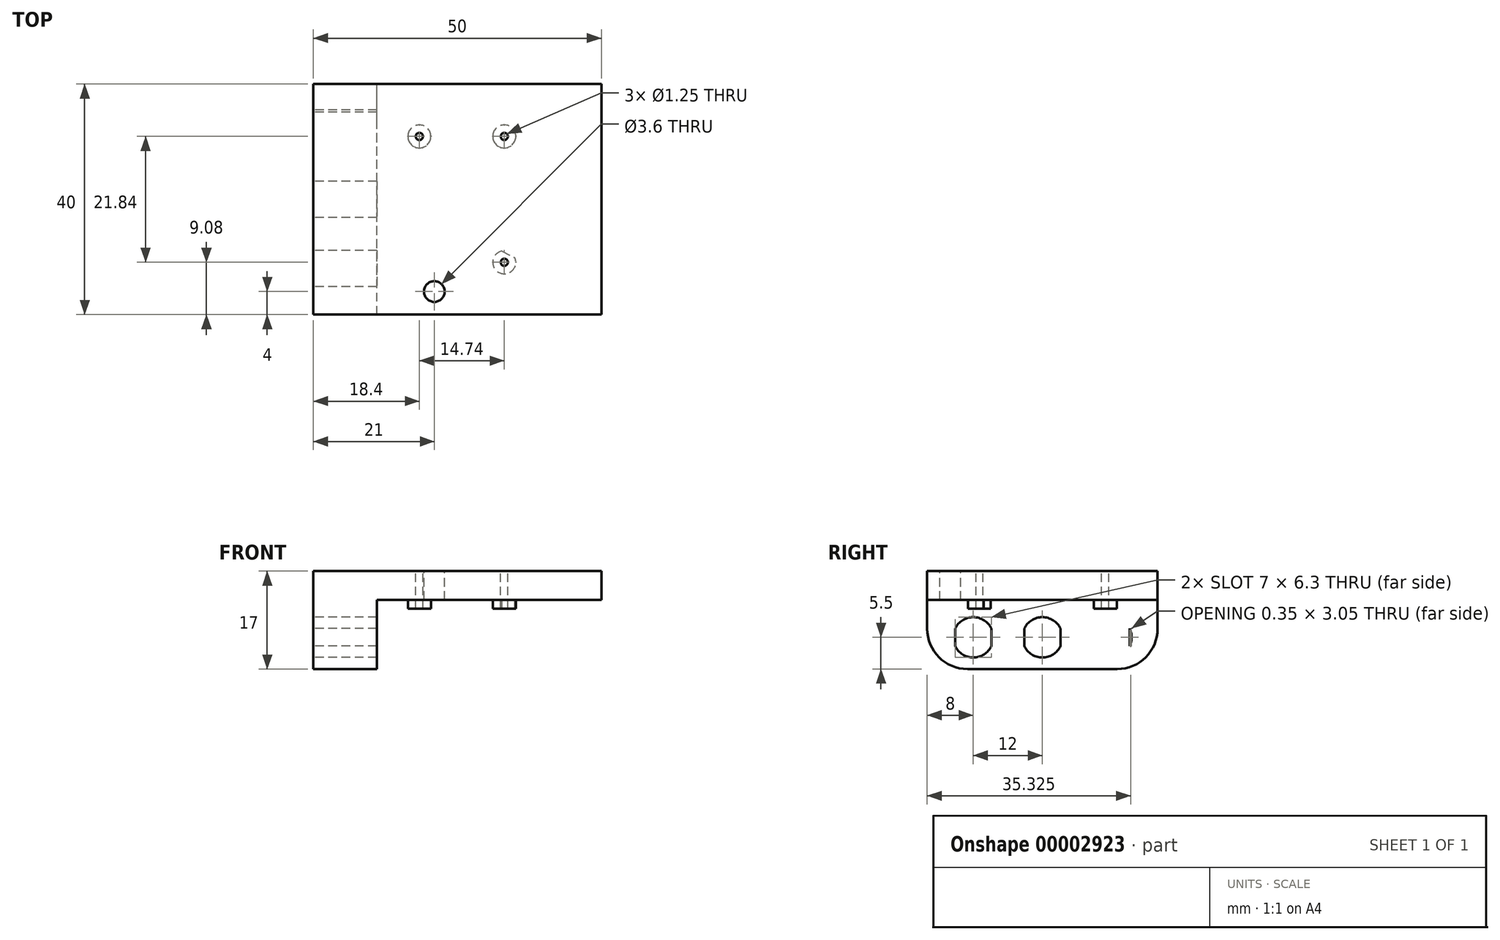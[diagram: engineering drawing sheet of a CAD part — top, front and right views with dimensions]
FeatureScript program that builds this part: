
annotation { "Feature Type Name" : "Feature", "Feature Type Description" : "" }
export const myFeature = defineFeature(function(context is Context, id is Id, definition is map)
    precondition{}
    {
        {
            var Q0;
            Q0=qCreatedBy(makeId("Top.planeOp"),FACE);
            var sketch = newSketch(context, id + "F0", { "sketchPlane" : qUnion([Q0])});
            skLineSegment(sketch, "E0.rect.bottom", {"start": v(25, 20) * mm, "end": v(-25, 20) * mm});
            skLineSegment(sketch, "E0.rect.top", {"start": v(25, -20) * mm, "end": v(-25, -20) * mm});
            skLineSegment(sketch, "E0.rect.left", {"start": v(25, 20) * mm, "end": v(25, -20) * mm});
            skLineSegment(sketch, "E0.rect.right", {"start": v(-25, 20) * mm, "end": v(-25, -20) * mm});
            skPoint(sketch, "E0.rect.middle", {"position": v(0, 0) * mm});
            skSolve(sketch);
        }
        {
            var Q0;
            Q0=makeQuery(id+"F0.imprint","IMPRINT",FACE,{"disambiguationData":[TD([[makeQuery(id+"F0.imprint","IMPRINT",EDGE,{"derivedFrom":sQuery(id+"F0.wireOp",EDGE,"E0.rect.bottom")}),1.0]])]});
            extrude(context, id + "F1", {"entities" : qUnion([Q0]), "depth" : 5 * mm});
        }
        {
            var Q0;
            Q0=makeQuery(id+"F1.opExtrude","CAP_FACE",FACE,{"disambiguationData":[OSD([sQuery(id+"F0.wireOp",EDGE,"E0.rect.bottom"),sQuery(id+"F0.wireOp",EDGE,"E0.rect.top"),sQuery(id+"F0.wireOp",EDGE,"E0.rect.left"),sQuery(id+"F0.wireOp",EDGE,"E0.rect.right")])],"isStart":false});
            var sketch = newSketch(context, id + "F2", { "sketchPlane" : qUnion([Q0])});
            skCircle(sketch, "E1", {"center": v(8.14, -10.92) * mm, "radius": 0.63 * mm});
            skCircle(sketch, "E2", {"center": v(8.14, 10.92) * mm, "radius": 0.63 * mm});
            skCircle(sketch, "E3", {"center": v(-6.6, 10.92) * mm, "radius": 0.63 * mm});
            skCircle(sketch, "E4", {"center": v(-4, -16) * mm, "radius": 1.8 * mm});
            skSolve(sketch);
        }
        {
            var Q0;
            Q0 = qSketchRegion(id + "F2", true);
            extrude(context, id + "F3", {"entities" : qUnion([Q0]), "operationType" : NewBodyOperationType.REMOVE, "oppositeDirection" : true, "depth" : 25 * mm});
        }
        {
            var Q0;
            Q0=makeQuery(id+"F1.opExtrude","CAP_FACE",FACE,{"disambiguationData":[OSD([sQuery(id+"F0.wireOp",EDGE,"E0.rect.bottom"),sQuery(id+"F0.wireOp",EDGE,"E0.rect.top"),sQuery(id+"F0.wireOp",EDGE,"E0.rect.left"),sQuery(id+"F0.wireOp",EDGE,"E0.rect.right")])],"isStart":true});
            var sketch = newSketch(context, id + "F4", { "sketchPlane" : qUnion([Q0])});
            skLineSegment(sketch, "E5.bottom", {"start": v(-25, 20) * mm, "end": v(-14, 20) * mm});
            skLineSegment(sketch, "E5.top", {"start": v(-25, -20) * mm, "end": v(-14, -20) * mm});
            skLineSegment(sketch, "E5.left", {"start": v(-25, 20) * mm, "end": v(-25, -20) * mm});
            skLineSegment(sketch, "E5.right", {"start": v(-14, 20) * mm, "end": v(-14, -20) * mm});
            skSolve(sketch);
        }
        {
            var Q0;
            Q0 = qSketchRegion(id + "F4", true);
            extrude(context, id + "F5", {"entities" : qUnion([Q0]), "operationType" : NewBodyOperationType.ADD, "depth" : 12 * mm});
        }
        {
            var Q0;
            Q0=makeQuery(id+"F1.opExtrude","CAP_FACE",FACE,{"disambiguationData":[OSD([sQuery(id+"F0.wireOp",EDGE,"E0.rect.bottom"),sQuery(id+"F0.wireOp",EDGE,"E0.rect.top"),sQuery(id+"F0.wireOp",EDGE,"E0.rect.left"),sQuery(id+"F0.wireOp",EDGE,"E0.rect.right")])],"isStart":true});
            var sketch = newSketch(context, id + "F6", { "sketchPlane" : qUnion([Q0])});
            skCircle(sketch, "E6", {"center": v(8.14, 10.92) * mm, "radius": 2 * mm});
            skCircle(sketch, "E7", {"center": v(8.14, 10.92) * mm, "radius": 0.62 * mm});
            skCircle(sketch, "E8", {"center": v(8.14, -10.92) * mm, "radius": 0.62 * mm});
            skCircle(sketch, "E9", {"center": v(8.14, -10.92) * mm, "radius": 2 * mm});
            skCircle(sketch, "E10", {"center": v(-6.6, -10.92) * mm, "radius": 0.62 * mm});
            skCircle(sketch, "E11", {"center": v(-6.6, -10.92) * mm, "radius": 2 * mm});
            skLineSegment(sketch, "E12", {"start": v(7.75, 8.96) * mm, "end": v(9.99, 10.15) * mm});
            skSolve(sketch);
        }
        {
            var Q0;
            Q0=makeQuery(id+"F6.imprint","IMPRINT",FACE,{"disambiguationData":[TD([[makeQuery(id+"F6.imprint","IMPRINT",EDGE,{"derivedFrom":sQuery(id+"F6.wireOp",EDGE,"E7")}),1.0]])]});
            var Q1;
            Q1=makeQuery(id+"F6.imprint","IMPRINT",FACE,{"disambiguationData":[TD([[makeQuery(id+"F6.imprint","IMPRINT",EDGE,{"derivedFrom":sQuery(id+"F6.wireOp",EDGE,"E8")}),1.0]])]});
            var Q2;
            Q2=makeQuery(id+"F6.imprint","IMPRINT",FACE,{"disambiguationData":[TD([[makeQuery(id+"F6.imprint","IMPRINT",EDGE,{"derivedFrom":sQuery(id+"F6.wireOp",EDGE,"E10")}),1.0]])]});
            extrude(context, id + "F7", {"entities" : qUnion([Q0, Q1, Q2]), "operationType" : NewBodyOperationType.ADD, "depth" : 1.5 * mm});
        }
        {
            var Q0;
            Q0=makeQuery(id+"F5.boolean.opBoolean","MERGE",FACE,{"derivedFrom":[makeQuery(id+"F1.opExtrude","SWEPT_FACE",FACE,{"disambiguationData":[OSD([sQuery(id+"F0.wireOp",EDGE,"E0.rect.right")])]}),makeQuery(id+"F5.opExtrude","SWEPT_FACE",FACE,{"disambiguationData":[OSD([sQuery(id+"F4.wireOp",EDGE,"E5.left")])]})]});
            var sketch = newSketch(context, id + "F8", { "sketchPlane" : qUnion([Q0])});
            skCircle(sketch, "E13", {"center": v(0, -6.5) * mm, "radius": 3.5 * mm});
            skLineSegment(sketch, "E14.rect.bottom", {"start": v(-3.15, -3.52) * mm, "end": v(3.15, -3.52) * mm});
            skLineSegment(sketch, "E14.rect.top", {"start": v(-3.15, -9.48) * mm, "end": v(3.15, -9.48) * mm});
            skLineSegment(sketch, "E14.rect.left", {"start": v(-3.15, -3.52) * mm, "end": v(-3.15, -9.48) * mm});
            skLineSegment(sketch, "E14.rect.right", {"start": v(3.15, -3.52) * mm, "end": v(3.15, -9.48) * mm});
            skCircle(sketch, "E15", {"center": v(12, -6.5) * mm, "radius": 3.5 * mm});
            skCircle(sketch, "E16", {"center": v(-12, -6.5) * mm, "radius": 3.5 * mm});
            skLineSegment(sketch, "E17.rect.bottom", {"start": v(-15.15, -1.66) * mm, "end": v(-8.85, -1.66) * mm});
            skLineSegment(sketch, "E17.rect.top", {"start": v(-15.15, -11.34) * mm, "end": v(-8.85, -11.34) * mm});
            skLineSegment(sketch, "E17.rect.left", {"start": v(-15.15, -1.66) * mm, "end": v(-15.15, -11.34) * mm});
            skLineSegment(sketch, "E17.rect.right", {"start": v(-8.85, -1.66) * mm, "end": v(-8.85, -11.34) * mm});
            skLineSegment(sketch, "E18.rect.bottom", {"start": v(8.85, -2.3) * mm, "end": v(15.15, -2.3) * mm});
            skLineSegment(sketch, "E18.rect.top", {"start": v(8.85, -10.7) * mm, "end": v(15.15, -10.7) * mm});
            skLineSegment(sketch, "E18.rect.left", {"start": v(8.85, -2.3) * mm, "end": v(8.85, -10.7) * mm});
            skLineSegment(sketch, "E18.rect.right", {"start": v(15.15, -2.3) * mm, "end": v(15.15, -10.7) * mm});
            skSolve(sketch);
        }
        {
            var Q0;
            {var subQ1=sQuery(id+"F8.wireOp",EDGE,"E16");var subQ4=sQuery(id+"F8.wireOp",EDGE,"E17.rect.left");var subQ6=makeQuery(id+"F8.imprint","INTERSECT",VERTEX,{"disambiguationData":[OD(0.0)],"derivedFrom":[subQ1,subQ4]});Q0=makeQuery(id+"F8.imprint","IMPRINT",FACE,{"disambiguationData":[TD([[makeQuery(id+"F8.imprint","IMPRINT",EDGE,{"disambiguationData":[TD([[subQ6,1.0]])],"derivedFrom":subQ1}),1.0]])]});}
            var Q1;
            {var subQ1=sQuery(id+"F8.wireOp",EDGE,"E13");var subQ10=sQuery(id+"F8.wireOp",EDGE,"E14.rect.bottom");var subQ12=makeQuery(id+"F8.imprint","INTERSECT",VERTEX,{"disambiguationData":[OD(0.0)],"derivedFrom":[subQ1,subQ10]});Q1=makeQuery(id+"F8.imprint","IMPRINT",FACE,{"disambiguationData":[TD([[makeQuery(id+"F8.imprint","IMPRINT",EDGE,{"disambiguationData":[TD([[subQ12,1.0]])],"derivedFrom":subQ1}),1.0]])]});}
            var Q2;
            {var subQ0=sQuery(id+"F8.wireOp",EDGE,"E14.rect.bottom");var subQ1=sQuery(id+"F8.wireOp",EDGE,"E13");var subQ3=makeQuery(id+"F8.imprint","INTERSECT",VERTEX,{"disambiguationData":[OD(0.0)],"derivedFrom":[subQ1,subQ0]});Q2=makeQuery(id+"F8.imprint","IMPRINT",FACE,{"disambiguationData":[TD([[makeQuery(id+"F8.imprint","IMPRINT",EDGE,{"disambiguationData":[TD([[subQ3,-1.0]])],"derivedFrom":subQ1}),1.0]])]});}
            var Q3;
            {var subQ0=sQuery(id+"F8.wireOp",EDGE,"E14.rect.top");var subQ1=sQuery(id+"F8.wireOp",EDGE,"E13");var subQ3=makeQuery(id+"F8.imprint","INTERSECT",VERTEX,{"disambiguationData":[OD(0.0)],"derivedFrom":[subQ1,subQ0]});Q3=makeQuery(id+"F8.imprint","IMPRINT",FACE,{"disambiguationData":[TD([[makeQuery(id+"F8.imprint","IMPRINT",EDGE,{"disambiguationData":[TD([[subQ3,-1.0]])],"derivedFrom":subQ1}),1.0]])]});}
            var Q4;
            {var subQ1=sQuery(id+"F8.wireOp",EDGE,"E15");var subQ4=sQuery(id+"F8.wireOp",EDGE,"E18.rect.left");var subQ6=makeQuery(id+"F8.imprint","INTERSECT",VERTEX,{"disambiguationData":[OD(0.0)],"derivedFrom":[subQ1,subQ4]});Q4=makeQuery(id+"F8.imprint","IMPRINT",FACE,{"disambiguationData":[TD([[makeQuery(id+"F8.imprint","IMPRINT",EDGE,{"disambiguationData":[TD([[subQ6,1.0]])],"derivedFrom":subQ1}),1.0]])]});}
            extrude(context, id + "F9", {"entities" : qUnion([Q0, Q1, Q2, Q3, Q4]), "operationType" : NewBodyOperationType.REMOVE, "oppositeDirection" : true, "depth" : 12 * mm});
        }
        {
            var Q0;
            Q0=makeQuery(id+"F5.opExtrude","CAP_EDGE",EDGE,{"disambiguationData":[OSD([sQuery(id+"F4.wireOp",EDGE,"E5.top")])],"isStart":false});
            var Q1;
            Q1=makeQuery(id+"F5.opExtrude","CAP_EDGE",EDGE,{"disambiguationData":[OSD([sQuery(id+"F4.wireOp",EDGE,"E5.bottom")])],"isStart":false});
            fillet(context, id + "F10", {"entities" : qUnion([Q0, Q1]), "radius" : 7 * mm, "tangentPropagation" : true, "allowEdgeOverflow" : false});
        }
    });
